# Revit family: IS_Ceraplus_A4088_BIM_DE
name_source: partatom
category: Plumbing Fixtures
revit_build: Autodesk Revit MEP 2016 (Build: 20161004_0715(x64)
units: mm (PartAtom-declared; Revit-internal decimal feet)

## family parameters
Always vertical = No
Cut with Voids When Loaded = No
OmniClass Number = 23.45.55.17
OmniClass Title = Mixing Faucets
Part Type = Normal
Room Calculation Point = No
Round Connector Dimension = Use Diameter
Shared = No
Work Plane-Based = No

## types (1)
- A4088AA CERAPLUS thermostatic exposed shower mixer
    Accessories = www.idealstandard.de\ersatzteile
    AssetType = Fixed
    BIMObjectName = ISI_IdealStandard_ShowerThermostaticvalves_CERAPLUS_A4088AA
    BIMobject category = Taps & Mixers
    BOSUseNativeGeometries = 1
    BarCode = 4015413304740
    Brand = Ideal Standard
    Brand url = http://www.idealstandard.de
    CodePerformance = EN 1111, DIN 4109, Gruppe 1
    Color = Chrome
    ConnectionType = Plumbing
    Cost = 0 $
    CurrencyUnit = €
    CurrentRevision = 1
    Description = A4088AA CERAPLUS thermostatic exposed shower mixer
    DurationUnit = Jaar
    EAN code = https://4015413304740
    Edition number = 1
    ExpectedLife = 25
    FaucetFunction = thermostatic
    FaucetType = pillar
    Features = CERAPLUS thermostatic exposed shower mixer
    Finish = Chrome
    IFC Classification = Sanitary Terminal
    IfcExportAs = Sanitary terminal type
    IfcExportType = BRASSWARE SHOWER
    Installation instructions = http://www.idealstandard.de
    InstallationInstructions = www.idealstandard.de\produkte
    LinearUnits = millimetres
    MainColor = Chrome
    MaintenanceInformation = www.idealstandard.de
    Manufacturer = http://www.idealstandard.de
    Manufacturer name = Ideal Standard
    ManufacturerURL = http://www.idealstandard.de
    Material = Brass
    Material main = Brass
    Model = A4088AA
    ModelNumber = A4088AA
    ModelReference = A4088AA CERAPLUS thermostatic exposed shower mixer
    Name = ISI_IdealStandard_ShowerThermostaticvalves_CERAPLUS_A4088AA
    NettWeight = 3,065 kg
    Nominal height = 0
    Nominal width = 0
    NominalHeight = 70 mm
    NominalLength = 188 mm
    NominalWidth = 297 mm
    Product Guid = 8f31851c-f2d8-4180-a296-06f07b02fde0
    Product SKU = A4088
    Product certification = EN 1111, DIN 4109, Gruppe 1
    Product data url = https://bimobject.com
    Product family = CERAPLUS
    Product group = Shower Mixer
    Product name = CERAPLUS thermostatic exposed shower mixer
    Product url = http://www.idealstandard.de
    ProductInformation = www.idealstandard.de/produkte
    QR code = http://bimobject.com
    Shape = Sculptured
    Size = 297x188x70 mm
    Space = Internal
    SpareParts = www.idealstandard.de/ersatzteile
    Technical description = http://www.idealstandard.de
    TestPressure = 10 Bar
    URL = http://www.idealstandard.de
    Uniclass2015Code = Pr_40_20_87_80
    Uniclass2015Title = Shower thermostatic valves
    Uniclass2015Version = Products v1.1
    VolumeUnits = Litres
    Weight Net (Kg) = 3.07
    WorkingPressure = 1-5 Bar

## geometry (parser evidence)
native form markers: Blend x4, Sweep x1
no freeform markers — native parametric forms only
